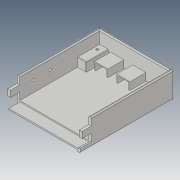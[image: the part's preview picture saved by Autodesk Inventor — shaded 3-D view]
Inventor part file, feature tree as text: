
AUTODESK INVENTOR PART (.ipt)
format: ipt  version: 2019 (Build 230136000, 136)  size: 433,152 bytes
history: native  units: mm
features: extrude x10, sketch x10, other x9, projected_geometry x5, direct_edit x3, fillet x2, plane x2, surface_op x1
ambient origin geometry x8: Origin, YZ Plane, XZ Plane, XY Plane, X Axis, Y Axis, Z Axis, Center Point
bodies: Solid1 (feature_tree)
feature tree (42):
  extrude  "Extrusion1"  Depth=170.0mm
  extrude  "Extrusion2"  Depth=5.0mm
  extrude  "Extrusion3"  Depth=25.0mm TaperAngle=0.0deg
  fillet  "Fillet1"  Radius=2.0mm
  extrude  "Extrusion4"  TaperAngle=0.0deg  [1 undecoded]
  extrude  "Extrusion5"  Depth=40.0mm
  fillet  "Fillet2"  [1 undecoded]
  plane  "Work Plane2"
  extrude  "Extrusion7"  Depth=35.0mm
  plane  "Work Plane1"
  extrude  "Extrusion8"  Depth=16.0mm TaperAngle=0.0deg
  surface_op  "Sculpt3"
  sketch  "Sketch8"  dims[d20=4.5mm d22=6.0mm]
  extrude  "Extrusion15"  Depth=6.0mm
  extrude  "Extrusion16"  Depth=7.0mm
  extrude  "Extrusion18"  Depth=1.0mm
  direct_edit  "Direct Edit1"
  direct_edit  "Direct Edit2"
  direct_edit  "Direct Edit3"
  sketch  "Sketch1"  dims[d0=135.0mm d1=170.0mm]
  sketch  "Sketch2"  dims[d2=46.7mm d3=0.0mm d4=5.0mm]
  projected_geometry  "Projected Loop1"
  sketch  "Sketch3"  dims[d5=38.7mm d6=0.0mm d7=25.0mm d8=0.0mm d9=2.0mm]
  projected_geometry  "Projected Loop2"
  sketch  "Sketch4"  dims[d10=0.0mm d11=0.0mm]
  sketch  "Sketch5"  dims[d12=16.0mm d13=40.0mm d14=0.0mm]
  sketch  "Sketch6"  dims[d15=0.0mm d16=35.0mm]
  sketch  "Sketch7"  dims[d17=16.0mm d18=16.0mm d19=0.0mm]
  sketch  "Sketch14"  dims[d23=4.5mm d24=7.0mm]
  projected_geometry  "Projected Loop10"
  sketch  "Sketch16"  dims[d26=12.0mm d27=0.0mm d28=1.0mm d29=4.5mm d30=4.5mm d31=30.8mm d34=90.0mm d37=0.0mm d38=0.0mm d39=-1.5mm d40=7.5mm d41=7.5mm d42=3.15mm d43=0.0mm d44=10.0mm d45=12.5mm d46=18.0mm d51=20.0mm d70=1.75mm d91=12.0mm d92=8.0mm d93=2.05mm d94=2.05mm d95=20.0mm d96=29.0mm d97=0.0mm d98=0.8mm d99=0.8mm d100=1.8mm d101=4.4mm d102=0.0mm d105=1.8mm d106=4.4mm d107=0.0mm d108=-0.3mm d109=-0.3mm d110=-0.3mm d111=-0.3mm d112=-0.3mm d113=-0.3mm d114=-0.1mm]
  projected_geometry  "Projected Loop13"
  projected_geometry  "Projected Loop14"
  other  "Composite3"
  other  "Srf3"
  other  "Size1"
  other  "Size2"
  other  "Size3"
  other  "Size4"
  other  "Size5"
  other  "Size6"
  other  "Size7"
note: 2 required parameter values undecoded (feature->parameter linkage not recoverable at this tier; creation-order binding heuristic only, values carry confidence <= 0.55)
